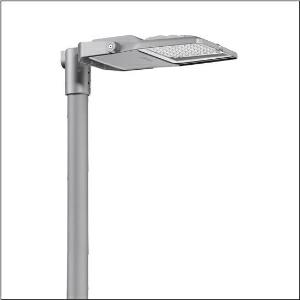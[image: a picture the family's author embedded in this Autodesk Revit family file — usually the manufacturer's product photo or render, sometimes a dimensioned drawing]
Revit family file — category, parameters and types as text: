
# Revit family: floodlight_fl_21_iq_mini___pl52_5xa7771c2d3a_33da
name_source: partatom
category: Lighting Fixtures
units: mm (PartAtom-declared; Revit-internal decimal feet)

## family parameters
Cut with Voids When Loaded = No
Host = Face
Light Source = No
Part Type = Normal
Room Calculation Point = No
Round Connector Dimension = Use Diameter
Shared = No

## types (1)
- --- (1 x LED, 12210 lm, 87.2 W, 3000K)
    Apparent Load = 87 VA
    CIE Flux Codes = 26 60 98 100 100
    Color Rendering = 70
    Color Temperature = 3000K
    Default Elevation = 1800 mm
    Description = Floodlight FL 21 iQ mini, floodlight, primary light control with lens, of PMMA, primary optical cover: protective disc, of toughened safety glass, transparent, light distribution: PL52, light emission: direct distribution, installation type: surface-mounted, LED, High Power LED, rated luminous flux: 12.210lm, luminous efficacy: 140lm/W, light colour: 730, colour temperature: 3000K, control: Auto-Match, Temp-Guard, Lumen-Switch, Night-Set, Smart-Wire, Light-Fading, Desk-Remote (wireless, voltage-free reading and setting of iQ features in the workshop via application-optimized NFC function/RFID function), optimised constant luminous flux control (CLO 2.0), with terminal, 6-pole, mains connection: 220..240V, AC, 50/60Hz, start of lifetime: 87W, end of service life: 92W, reduction: 40W, luminaire housing, of diecast aluminium, powder-coated, Siteco® metallic grey (DB 702S), corrosivity category C5 mid according to DIN EN ISO 12944, sealing non-destructively replaceable, please order mast flange separately, mast bracket, of steel, galvanised, powder-coated, Siteco® metallic grey (DB 702S), protection rating (complete): IP66, insulation class (complete): insulation class II (safety insulation), certification: CE, ENEC, VDE, protection symbol: D, impact resistance: IK08, permissible operating ambient temperature: -40..+40°C, permissible operating ambient temperature for outdoor applications: -40..+50°C, standard: DIN EN 12944, LABS conformity tested according to VDMA 24364:2018-05, packaging unit: 1 piece

Light Distribution: PL52
    Height = 70 mm
    Lamp = 1 x LED
    Lamp Light Flux = 12210 lm
    Lamp Power = 87.2 W
    Lamp count = 1
    Length = 485 mm
    Luminous efficacy = 140 lm/W
    Manufacturer = Siteco
    ModVariant = No
    Model = 5XA7771C2D3A
    Number of Poles = 1
    OnlyDefault = Yes
    Power Factor = 1
    Product Name = Floodlight FL 21 iQ mini | PL52
    Product group = floodlight | pylon annexe
    ProductGroupID = 6200
    Protection Class = Protection class II
    Protection Degree = IP 66
    RLX_Detail_Level = 1
    RLX_Emergency_Light_Flux = 0 lm
    RLX_Emergency_Type = 0
    RLX_Emergency_Type_DB = No
    RlxData = <blob elided: 101477 chars, md5=5424173e>
    Socket = socket
    Standby Power = 0 W
    System Light Flux = 12210 lm
    System Power = 87 W
    Type Comments = factory setting: luminous flux: 100 % | dim-lin: 254 | 456 mA
    Type Image = l_1007125.jpg
    URL = http://relux.com
    VarID = @adj_114707
    Voltage = 0 V
    Weight = 0.00 kg
    Width = 337 mm

## geometry (parser evidence)
native form markers: Blend x4, Sweep x12
no freeform markers — native parametric forms only
